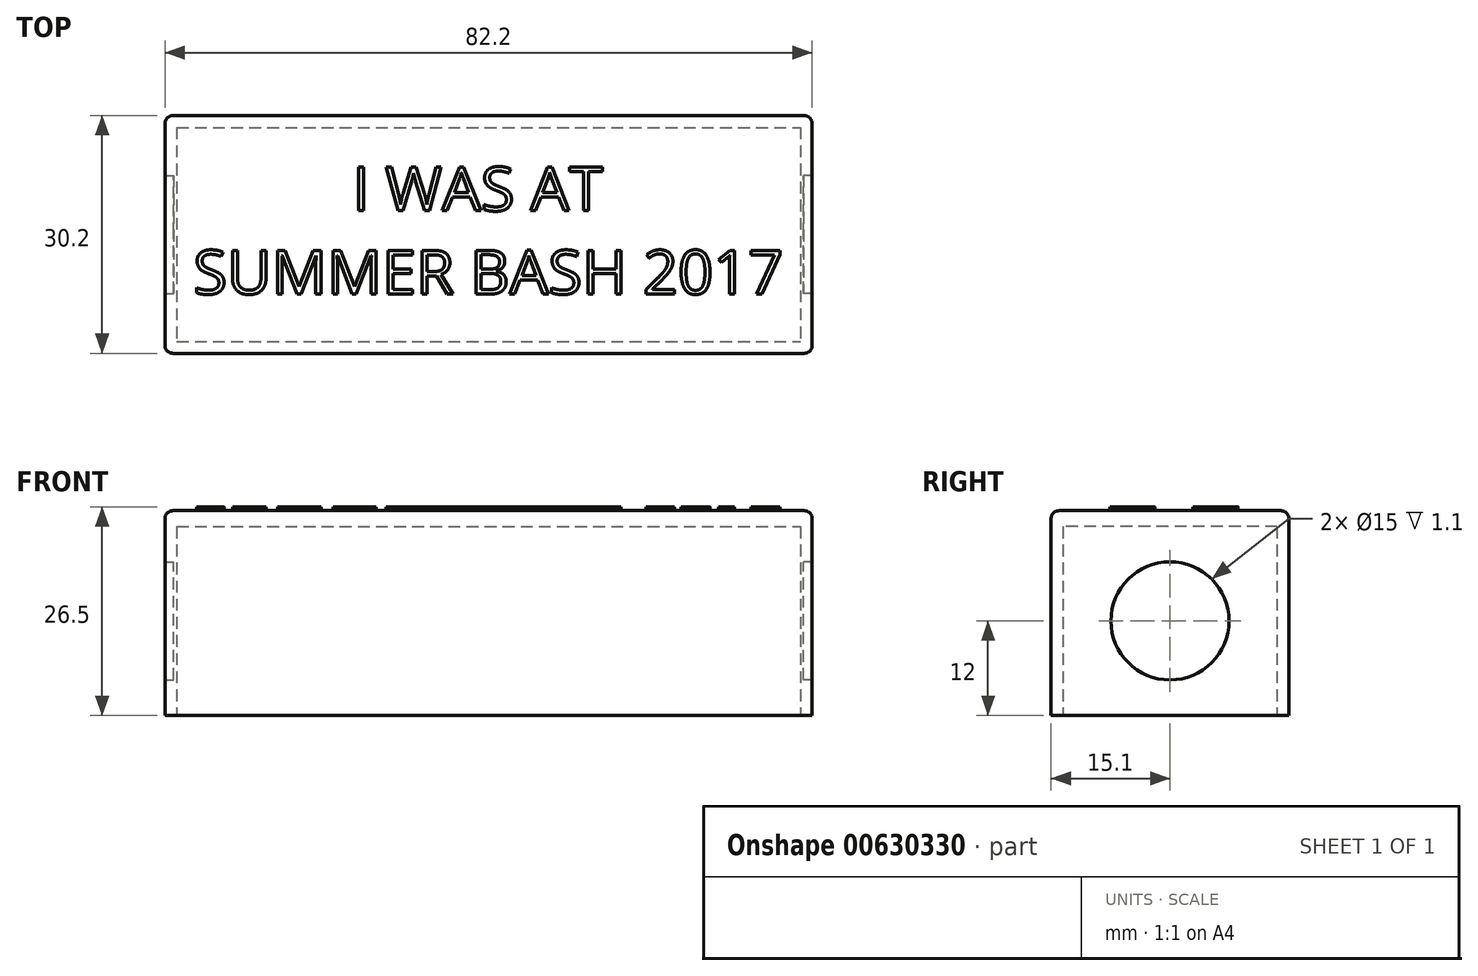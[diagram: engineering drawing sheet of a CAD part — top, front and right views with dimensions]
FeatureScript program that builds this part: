
annotation { "Feature Type Name" : "Feature", "Feature Type Description" : "" }
export const myFeature = defineFeature(function(context is Context, id is Id, definition is map)
    precondition{}
    {
        {
            var Q0;
            Q0=qCreatedBy(makeId("Top.planeOp"),FACE);
            var sketch = newSketch(context, id + "F0", { "sketchPlane" : qUnion([Q0])});
            skLineSegment(sketch, "E0.bottom", {"start": v(-39.6, 13.6) * mm, "end": v(39.6, 13.6) * mm});
            skLineSegment(sketch, "E0.top", {"start": v(-39.6, -13.6) * mm, "end": v(39.6, -13.6) * mm});
            skLineSegment(sketch, "E0.left", {"start": v(-39.6, 13.6) * mm, "end": v(-39.6, -13.6) * mm});
            skLineSegment(sketch, "E0.right", {"start": v(39.6, 13.6) * mm, "end": v(39.6, -13.6) * mm});
            skPoint(sketch, "E0.middle", {"position": v(0, 0) * mm});
            skLineSegment(sketch, "E1.0", {"start": v(-41.1, 15.1) * mm, "end": v(41.1, 15.1) * mm});
            skLineSegment(sketch, "E1.1", {"start": v(-41.1, 15.1) * mm, "end": v(-41.1, -15.1) * mm});
            skLineSegment(sketch, "E1.2", {"start": v(-41.1, -15.1) * mm, "end": v(41.1, -15.1) * mm});
            skLineSegment(sketch, "E1.3", {"start": v(41.1, 15.1) * mm, "end": v(41.1, -15.1) * mm});
            skSolve(sketch);
        }
        {
            var Q0;
            Q0 = qSketchRegion(id + "F0", true);
            extrude(context, id + "F1", {"entities" : qUnion([Q0]), "depth" : 24 * mm, "offsetDistance" : 25 * mm});
        }
        {
            var Q0;
            Q0=qCreatedBy(makeId("Top.planeOp"),FACE);
            var sketch = newSketch(context, id + "F2", { "sketchPlane" : qUnion([Q0])});
            skLineSegment(sketch, "E2.bottom", {"start": v(-41.1, -15.1) * mm, "end": v(41.1, -15.1) * mm});
            skLineSegment(sketch, "E2.top", {"start": v(-41.1, 15.1) * mm, "end": v(41.1, 15.1) * mm});
            skLineSegment(sketch, "E2.left", {"start": v(-41.1, -15.1) * mm, "end": v(-41.1, 15.1) * mm});
            skLineSegment(sketch, "E2.right", {"start": v(41.1, -15.1) * mm, "end": v(41.1, 15.1) * mm});
            skPoint(sketch, "E2.middle", {"position": v(0, 0) * mm});
            skSolve(sketch);
        }
        {
            var Q0;
            Q0 = qSketchRegion(id + "F2", true);
            extrude(context, id + "F3", {"entities" : qUnion([Q0]), "operationType" : NewBodyOperationType.ADD, "depth" : 26 * mm, "offsetDistance" : 25 * mm, "hasSecondDirection" : true, "secondDirectionOppositeDirection" : false, "secondDirectionDepth" : 24 * mm});
        }
        {
            var Q0;
            Q0=makeQuery(id+"F3.opExtrude","CAP_EDGE",EDGE,{"disambiguationData":[OSD([sQuery(id+"F2.wireOp",EDGE,"E2.left")])],"isStart":false});
            var Q1;
            Q1=makeQuery(id+"F3.opExtrude","CAP_EDGE",EDGE,{"disambiguationData":[OSD([sQuery(id+"F2.wireOp",EDGE,"E2.bottom")])],"isStart":false});
            var Q2;
            Q2=makeQuery(id+"F3.opExtrude","CAP_EDGE",EDGE,{"disambiguationData":[OSD([sQuery(id+"F2.wireOp",EDGE,"E2.right")])],"isStart":false});
            var Q3;
            Q3=makeQuery(id+"F3.opExtrude","CAP_EDGE",EDGE,{"disambiguationData":[OSD([sQuery(id+"F2.wireOp",EDGE,"E2.top")])],"isStart":false});
            var Q4;
            Q4=makeQuery(id+"F3.boolean.opBoolean","MERGE",EDGE,{"derivedFrom":[makeQuery(id+"F1.opExtrude","SWEPT_EDGE",EDGE,{"disambiguationData":[OSD([sQuery(id+"F0.wireOp",EDGE,"E1.2"),sQuery(id+"F0.wireOp",EDGE,"E1.3")])]}),makeQuery(id+"F3.opExtrude","SWEPT_EDGE",EDGE,{"disambiguationData":[OSD([sQuery(id+"F2.wireOp",EDGE,"E2.bottom"),sQuery(id+"F2.wireOp",EDGE,"E2.right")])]})]});
            var Q5;
            Q5=makeQuery(id+"F3.boolean.opBoolean","MERGE",EDGE,{"derivedFrom":[makeQuery(id+"F1.opExtrude","SWEPT_EDGE",EDGE,{"disambiguationData":[OSD([sQuery(id+"F0.wireOp",EDGE,"E1.1"),sQuery(id+"F0.wireOp",EDGE,"E1.2")])]}),makeQuery(id+"F3.opExtrude","SWEPT_EDGE",EDGE,{"disambiguationData":[OSD([sQuery(id+"F2.wireOp",EDGE,"E2.bottom"),sQuery(id+"F2.wireOp",EDGE,"E2.left")])]})]});
            var Q6;
            Q6=makeQuery(id+"F3.boolean.opBoolean","MERGE",EDGE,{"derivedFrom":[makeQuery(id+"F1.opExtrude","SWEPT_EDGE",EDGE,{"disambiguationData":[OSD([sQuery(id+"F0.wireOp",EDGE,"E1.0"),sQuery(id+"F0.wireOp",EDGE,"E1.3")])]}),makeQuery(id+"F3.opExtrude","SWEPT_EDGE",EDGE,{"disambiguationData":[OSD([sQuery(id+"F2.wireOp",EDGE,"E2.top"),sQuery(id+"F2.wireOp",EDGE,"E2.right")])]})]});
            var Q7;
            Q7=makeQuery(id+"F3.boolean.opBoolean","MERGE",EDGE,{"derivedFrom":[makeQuery(id+"F1.opExtrude","SWEPT_EDGE",EDGE,{"disambiguationData":[OSD([sQuery(id+"F0.wireOp",EDGE,"E1.0"),sQuery(id+"F0.wireOp",EDGE,"E1.1")])]}),makeQuery(id+"F3.opExtrude","SWEPT_EDGE",EDGE,{"disambiguationData":[OSD([sQuery(id+"F2.wireOp",EDGE,"E2.top"),sQuery(id+"F2.wireOp",EDGE,"E2.left")])]})]});
            fillet(context, id + "F4", {"entities" : qUnion([Q0, Q1, Q2, Q3, Q4, Q5, Q6, Q7]), "radius" : 1 * mm, "tangentPropagation" : true, "allowEdgeOverflow" : false});
        }
        {
            var Q0;
            Q0=qCreatedBy(makeId("Front.planeOp"),FACE);
            var sketch = newSketch(context, id + "F5", { "sketchPlane" : qUnion([Q0])});
            skLineSegment(sketch, "E3", {"start": v(0, 0) * mm, "end": v(0, 12) * mm, "construction": true});
            skLineSegment(sketch, "E4", {"start": v(0, 12) * mm, "end": v(40, 12) * mm, "construction": true});
            skCircle(sketch, "E5", {"center": v(0, 12) * mm, "radius": 6 * mm});
            skSolve(sketch);
        }
        {
            var Q0;
            Q0 = qSketchRegion(id + "F5", true);
            extrude(context, id + "F6", {"entities" : qUnion([Q0]), "operationType" : NewBodyOperationType.REMOVE, "depth" : 50 * mm, "offsetDistance" : 25 * mm, "hasSecondDirection" : true, "secondDirectionOppositeDirection" : false, "secondDirectionDepth" : 40 * mm});
        }
        {
            var Q0;
            Q0 = qSketchRegion(id + "F5", true);
            extrude(context, id + "F7", {"entities" : qUnion([Q0]), "operationType" : NewBodyOperationType.REMOVE, "oppositeDirection" : true, "depth" : 50 * mm, "offsetDistance" : 25 * mm, "hasSecondDirection" : true, "secondDirectionOppositeDirection" : true, "secondDirectionDepth" : 40 * mm});
        }
        {
            var Q0;
            Q0=makeQuery(id+"F3.opExtrude","CAP_FACE",FACE,{"disambiguationData":[OSD([sQuery(id+"F2.wireOp",EDGE,"E2.bottom"),sQuery(id+"F2.wireOp",EDGE,"E2.top"),sQuery(id+"F2.wireOp",EDGE,"E2.left"),sQuery(id+"F2.wireOp",EDGE,"E2.right")])],"isStart":false});
            var sketch = newSketch(context, id + "F8", { "sketchPlane" : qUnion([Q0])});
            skText(sketch, "E6", { "text": "          I WAS AT\nSUMMER BASH 2017", "fontName": "OpenSans-Regular.ttf"});
            skPoint(sketch, "E7.middle", {"position": v(0, 0) * mm});
            const initialGuessF8  = {"E6": [-0.0375, 0.003, 1, 0, 0.0056]};
            skSetInitialGuess(sketch, initialGuessF8);
            skSolve(sketch);
        }
        {
            var Q0;
            Q0 = qSketchRegion(id + "F8", true);
            extrude(context, id + "F9", {"entities" : qUnion([Q0]), "operationType" : NewBodyOperationType.ADD, "depth" : .5 * mm, "offsetDistance" : 25 * mm});
        }
        {
            var Q0;
            Q0=qCreatedBy(makeId("Right.planeOp"),FACE);
            var sketch = newSketch(context, id + "F10", { "sketchPlane" : qUnion([Q0])});
            skLineSegment(sketch, "E8", {"start": v(0, 1.15) * mm, "end": v(0, 0) * mm, "construction": true});
            skLineSegment(sketch, "E9", {"start": v(0, 0) * mm, "end": v(0, 12) * mm, "construction": true});
            skLineSegment(sketch, "E10", {"start": v(0, 12) * mm, "end": v(30, 12) * mm, "construction": true});
            skCircle(sketch, "E11", {"center": v(0, 12) * mm, "radius": 7.5 * mm});
            skSolve(sketch);
        }
        {
            var Q0;
            Q0 = qSketchRegion(id + "F10", true);
            extrude(context, id + "F11", {"entities" : qUnion([Q0]), "operationType" : NewBodyOperationType.REMOVE, "depth" : 50 * mm, "offsetDistance" : 25 * mm, "hasSecondDirection" : true, "secondDirectionOppositeDirection" : false, "secondDirectionDepth" : 40 * mm});
        }
        {
            var Q0;
            Q0 = qSketchRegion(id + "F10", true);
            extrude(context, id + "F12", {"entities" : qUnion([Q0]), "operationType" : NewBodyOperationType.REMOVE, "oppositeDirection" : true, "depth" : 50 * mm, "offsetDistance" : 25 * mm, "hasSecondDirection" : true, "secondDirectionOppositeDirection" : true, "secondDirectionDepth" : 40 * mm});
        }
    });
